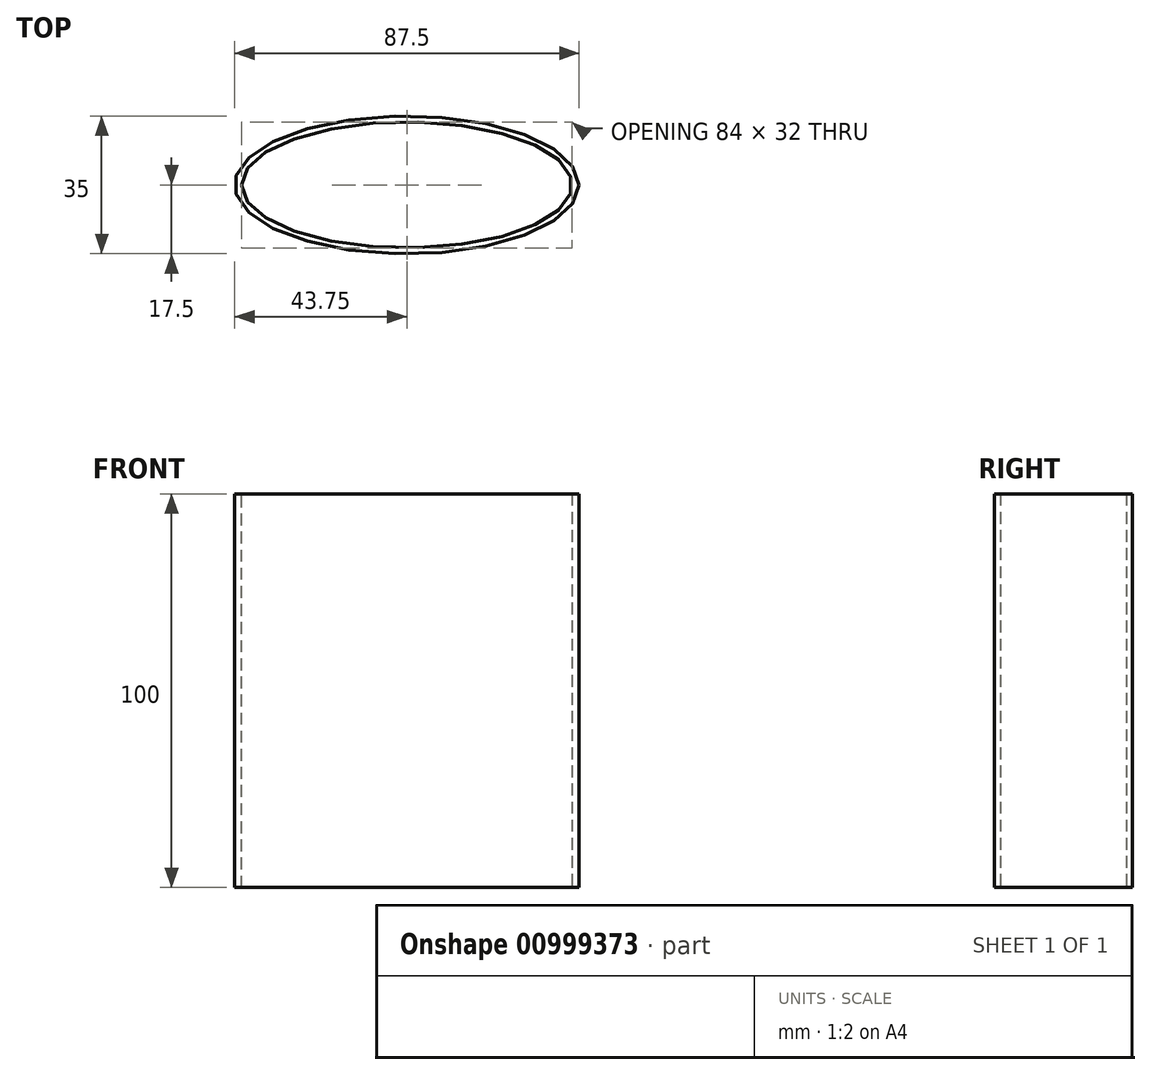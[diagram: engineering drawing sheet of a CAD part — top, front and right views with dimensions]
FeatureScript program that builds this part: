
annotation { "Feature Type Name" : "Feature", "Feature Type Description" : "" }
export const myFeature = defineFeature(function(context is Context, id is Id, definition is map)
    precondition{}
    {
        {
            var Q0;
            Q0=qCreatedBy(makeId("Top.planeOp"),FACE);
            var sketch = newSketch(context, id + "F0", { "sketchPlane" : qUnion([Q0])});
            skEllipse(sketch, "E0", {"center": v(0, 0) * mm, "majorRadius": 43.75 * mm, "minorRadius": 17.5 * mm, "majorAxis": v(1, 0)});
            skSolve(sketch);
        }
        {
            var Q0;
            Q0=makeQuery(id+"F0.imprint","IMPRINT",FACE,{"disambiguationData":[TD([[makeQuery(id+"F0.imprint","IMPRINT",EDGE,{"derivedFrom":sQuery(id+"F0.wireOp",EDGE,"E0")}),1.0]])]});
            extrude(context, id + "F1", {"entities" : qUnion([Q0]), "depth" : 100 * mm, "offsetDistance" : 25 * mm});
        }
        {
            var Q0;
            Q0=makeQuery(id+"F1.opExtrude","CAP_FACE",FACE,{"disambiguationData":[OSD([sQuery(id+"F0.wireOp",EDGE,"E0")])],"isStart":false});
            var sketch = newSketch(context, id + "F2", { "sketchPlane" : qUnion([Q0])});
            skEllipse(sketch, "E1", {"center": v(0, 0) * mm, "majorRadius": 42 * mm, "minorRadius": 16 * mm, "majorAxis": v(-1, 0)});
            skSolve(sketch);
        }
        {
            var Q0;
            Q0=makeQuery(id+"F2.imprint","IMPRINT",FACE,{"disambiguationData":[TD([[makeQuery(id+"F2.imprint","IMPRINT",EDGE,{"derivedFrom":sQuery(id+"F2.wireOp",EDGE,"E1")}),1.0]])]});
            var Q1;
            Q1=sQuery(id+"F2.wireOp",EDGE,"E1");
            extrude(context, id + "F3", {"entities" : qUnion([Q0]), "operationType" : NewBodyOperationType.REMOVE, "surfaceEntities" : qUnion([Q1]), "endBound" : BoundingType.THROUGH_ALL, "oppositeDirection" : true, "depth" : 25 * mm, "offsetDistance" : 25 * mm});
        }
    });
